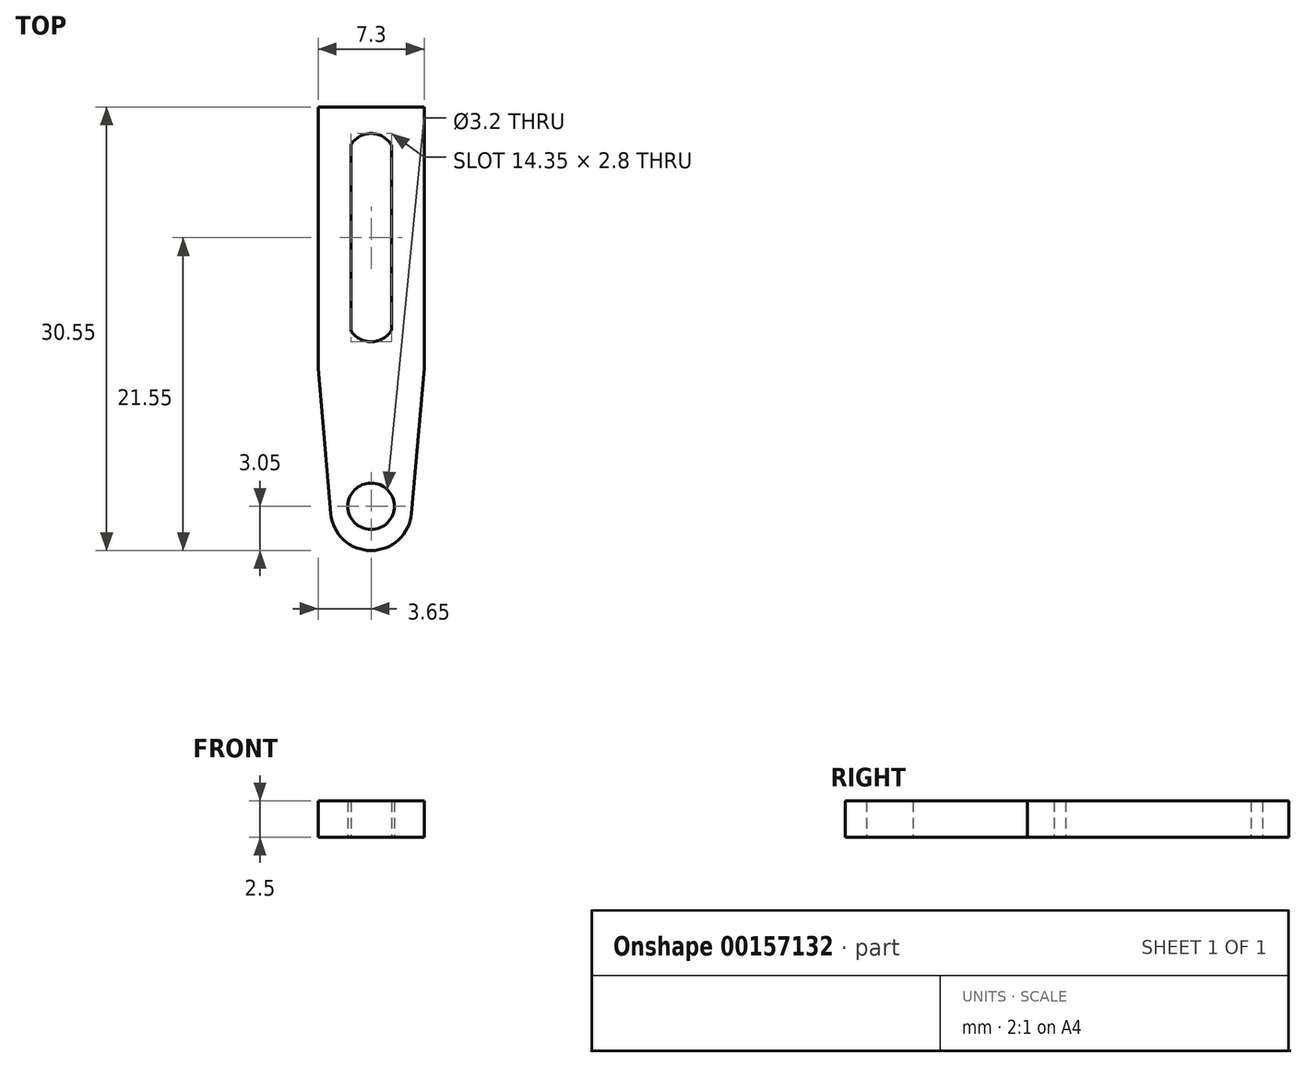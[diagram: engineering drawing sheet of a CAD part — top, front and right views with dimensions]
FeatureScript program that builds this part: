
annotation { "Feature Type Name" : "Feature", "Feature Type Description" : "" }
export const myFeature = defineFeature(function(context is Context, id is Id, definition is map)
    precondition{}
    {
        {
            var Q0;
            Q0=qCreatedBy(makeId("Top.planeOp"),FACE);
            var sketch = newSketch(context, id + "F0", { "sketchPlane" : qUnion([Q0])});
            skLineSegment(sketch, "E0.bottom", {"start": v(3.65, 9) * mm, "end": v(-3.65, 9) * mm});
            skLineSegment(sketch, "E0.top", {"start": v(3.65, -9) * mm, "end": v(-3.65, -9) * mm});
            skLineSegment(sketch, "E0.left", {"start": v(3.65, 9) * mm, "end": v(3.65, -9) * mm});
            skLineSegment(sketch, "E0.right", {"start": v(-3.65, 9) * mm, "end": v(-3.65, -9) * mm});
            skPoint(sketch, "E0.middle", {"position": v(0, 0) * mm});
            skLineSegment(sketch, "E1.bottom", {"start": v(1.4, 6.38) * mm, "end": v(-1.4, 6.38) * mm});
            skLineSegment(sketch, "E1.top", {"start": v(1.4, -6.38) * mm, "end": v(-1.4, -6.38) * mm});
            skLineSegment(sketch, "E1.left", {"start": v(1.4, 6.38) * mm, "end": v(1.4, -6.38) * mm});
            skLineSegment(sketch, "E1.right", {"start": v(-1.4, 6.38) * mm, "end": v(-1.4, -6.38) * mm});
            skArc(sketch, "E2", {"start": v(1.4, 6.38) * mm, "mid": v(0, 7.17) * mm, "end": v(-1.4, 6.38) * mm});
            skArc(sketch, "E3.MirrorCS", {"start": v(1.4, -6.38) * mm, "mid": v(0, -7.17) * mm, "end": v(-1.4, -6.38) * mm});
            skCircle(sketch, "E4", {"center": v(0, -18.5) * mm, "radius": 1.6 * mm});
            skLineSegment(sketch, "E5", {"start": v(-3.65, -9) * mm, "end": v(-2.78, -19) * mm});
            skLineSegment(sketch, "E6.MirrorCS", {"start": v(3.65, -9) * mm, "end": v(2.78, -19) * mm});
            skArc(sketch, "E7", {"start": v(-2.78, -19) * mm, "mid": v(0, -21.55) * mm, "end": v(2.78, -19) * mm});
            skSolve(sketch);
        }
        {
            var Q0;
            Q0=makeQuery(id+"F0.imprint","IMPRINT",FACE,{"disambiguationData":[TD([[makeQuery(id+"F0.imprint","IMPRINT",EDGE,{"derivedFrom":sQuery(id+"F0.wireOp",EDGE,"E0.bottom")}),1.0]])]});
            var Q1;
            Q1=makeQuery(id+"F0.imprint","IMPRINT",FACE,{"disambiguationData":[TD([[makeQuery(id+"F0.imprint","IMPRINT",EDGE,{"derivedFrom":sQuery(id+"F0.wireOp",EDGE,"E0.top")}),1.0]])]});
            extrude(context, id + "F1", {"entities" : qUnion([Q0, Q1]), "depth" : 2.5 * mm});
        }
    });
